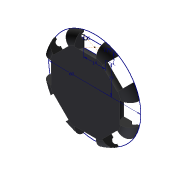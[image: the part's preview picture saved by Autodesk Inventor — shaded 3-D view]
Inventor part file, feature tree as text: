
AUTODESK INVENTOR PART (.ipt)
format: ipt  version: 2017 (Build 210142000, 142)  size: 195,072 bytes
history: native  units: mm
features: sketch x2, extrude x2, revolve x1, fillet x1, pattern_circular x1, projected_geometry x1
ambient origin geometry x8: Origin, YZ Plane, XZ Plane, XY Plane, X Axis, Y Axis, Z Axis, Center Point
bodies: Solid1 (feature_tree)
feature tree (8):
  sketch  "Sketch1"  dims[d0=60.0mm d1=14.0mm]
  extrude  "Extrusion1"  Depth=14.0mm
  revolve  "Revolution1"  [1 undecoded]
  extrude  "Extrusion2"  Depth=6.0mm
  fillet  "Fillet1"  Radius=5.0mm
  pattern_circular  "Circular Pattern1"  [2 undecoded]
  sketch  "Sketch2"  dims[d2=7.0mm d3=19.0mm d4=5.0mm d5=5.0mm d6=1.75mm d7=1.75mm d8=6.0mm d9=0.0mm d10=90.0deg d11=12.0mm d12=0.0mm d13=6.0mm d14=80.0mm d15=360.0deg]
  projected_geometry  "Projected Loop1"
note: 3 required parameter values undecoded (feature->parameter linkage not recoverable at this tier; creation-order binding heuristic only, values carry confidence <= 0.55)